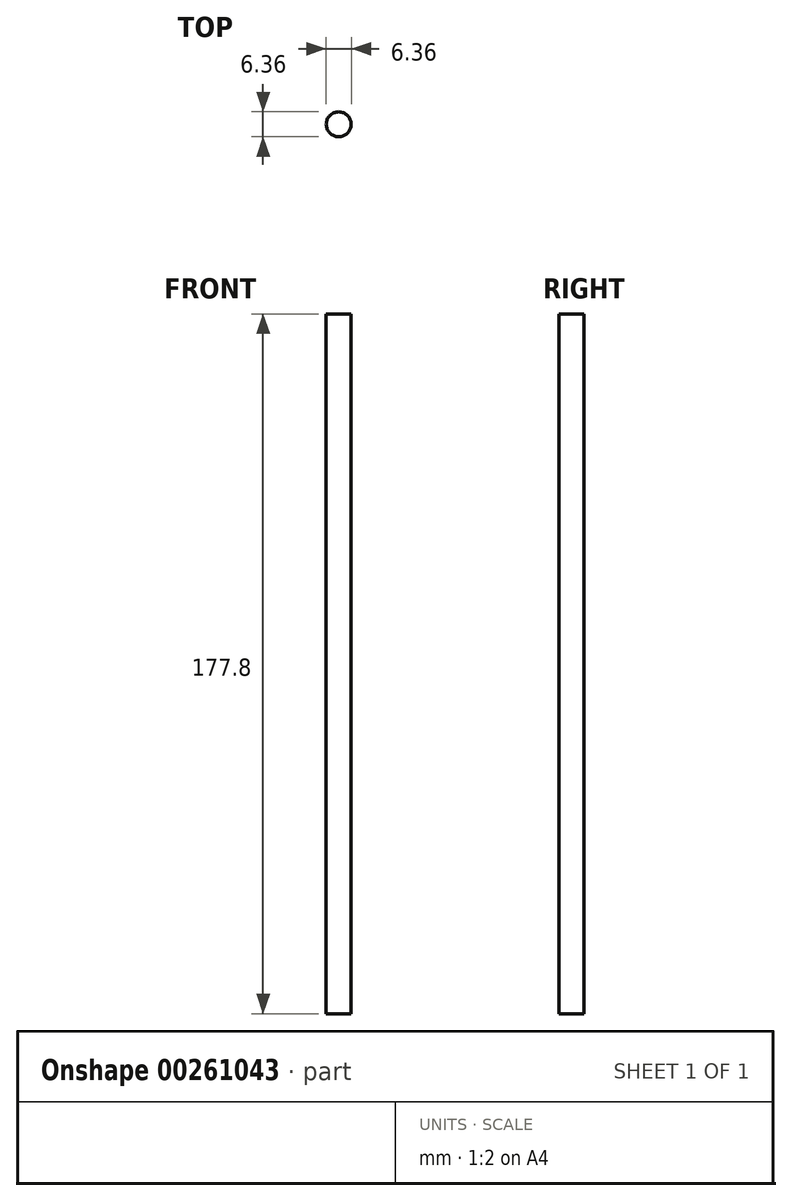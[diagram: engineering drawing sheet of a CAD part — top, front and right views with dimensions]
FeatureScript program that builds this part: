
annotation { "Feature Type Name" : "Feature", "Feature Type Description" : "" }
export const myFeature = defineFeature(function(context is Context, id is Id, definition is map)
    precondition{}
    {
        {
            var Q0;
            Q0=qCreatedBy(makeId("Top.planeOp"),FACE);
            var sketch = newSketch(context, id + "F0", { "sketchPlane" : qUnion([Q0])});
            skCircle(sketch, "E0", {"center": v(0, 0) * mm, "radius": 3.18 * mm});
            skSolve(sketch);
        }
        {
            var Q0;
            Q0=qSketchRegion(id+"F0",true);
            extrude(context, id + "F1", {"entities" : qUnion([Q0]), "depth" : 177.8 * mm});
        }
    });
